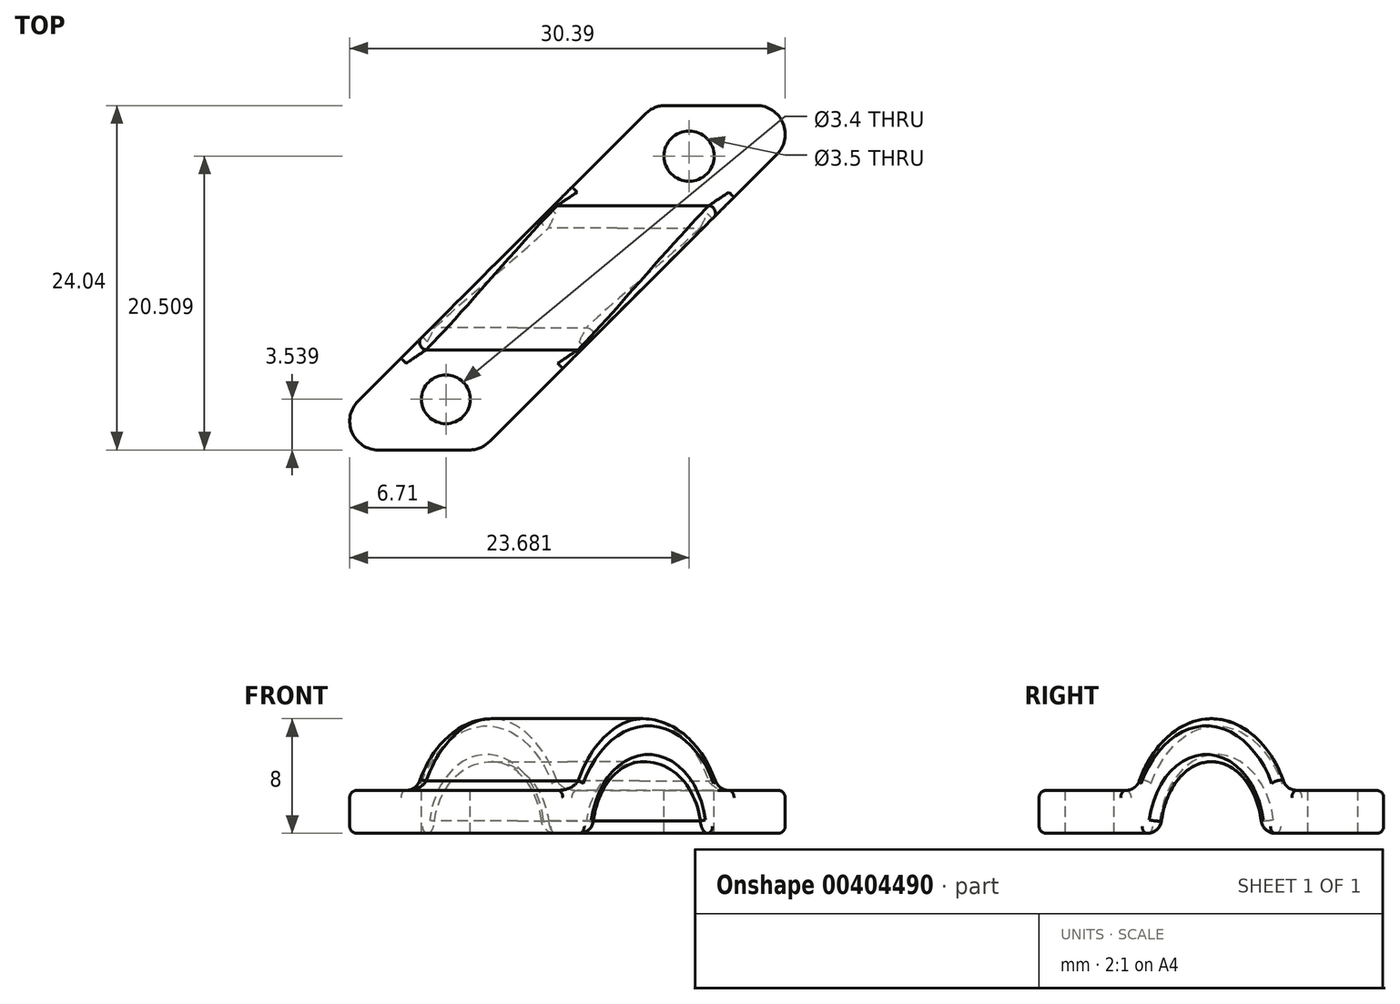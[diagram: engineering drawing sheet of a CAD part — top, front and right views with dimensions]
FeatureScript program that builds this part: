
annotation { "Feature Type Name" : "Feature", "Feature Type Description" : "" }
export const myFeature = defineFeature(function(context is Context, id is Id, definition is map)
    precondition{}
    {
        {
            var Q0;
            Q0=qCreatedBy(makeId("Top.planeOp"),FACE);
            var sketch = newSketch(context, id + "F0", { "sketchPlane" : qUnion([Q0])});
            skLineSegment(sketch, "E0", {"start": v(0, -18.35) * mm, "end": v(0, 0) * mm, "construction": true});
            skLineSegment(sketch, "E1", {"start": v(0, 0) * mm, "end": v(0, 0) * mm});
            skLineSegment(sketch, "E2", {"start": v(0, 0) * mm, "end": v(30, 30) * mm, "construction": true});
            skCircle(sketch, "E3", {"center": v(15, 8.92) * mm, "radius": 1.7 * mm});
            skPoint(sketch, "E3.centerSnap0", {"position": v(15, 15) * mm});
            skCircle(sketch, "E4", {"center": v(31.97, 25.89) * mm, "radius": 1.75 * mm});
            skLineSegment(sketch, "E5", {"start": v(6.42, 0.34) * mm, "end": v(37.39, 31.3) * mm, "construction": true});
            skLineSegment(sketch, "E6", {"start": v(21, 8.92) * mm, "end": v(15, 8.92) * mm});
            skLineSegment(sketch, "E7", {"start": v(15, 8.92) * mm, "end": v(9, 8.92) * mm});
            skSolve(sketch);
        }
        {
            var Q0;
            Q0=sQuery(id+"F0.wireOp",EDGE,"E5");
            var Q1;
            Q1=qCreatedBy(makeId("Top.planeOp"),FACE);
            cPlane(context, id + "F1", {"entities" : qUnion([Q0, Q1]), "cplaneType" : CPlaneType.LINE_ANGLE, "offset" : 25 * mm, "angle" : 90 * degree, "width" : 150 * mm, "height" : 150 * mm});
        }
        {
            var Q0;
            Q0=qCreatedBy(id+"F1.planeOp",FACE);
            var sketch = newSketch(context, id + "F2", { "sketchPlane" : qUnion([Q0])});
            skPoint(sketch, "E8.0", {"position": v(-16.91, 0) * mm});
            skPoint(sketch, "E9.0", {"position": v(-40.91, 0) * mm});
            skLineSegment(sketch, "E10", {"start": v(-40.91, 0) * mm, "end": v(-40.91, 4.4) * mm, "construction": true});
            skLineSegment(sketch, "E11", {"start": v(-16.91, 0) * mm, "end": v(-16.91, 4.43) * mm, "construction": true});
            skLineSegment(sketch, "E12.bottom", {"start": v(-11.91, 3) * mm, "end": v(-21.5, 3) * mm});
            skLineSegment(sketch, "E12.top", {"start": v(-11.91, 0) * mm, "end": v(-23.91, 0) * mm});
            skLineSegment(sketch, "E12.left", {"start": v(-11.91, 3) * mm, "end": v(-11.91, 0) * mm});
            skLineSegment(sketch, "E12.right", {"start": v(-45.91, 3) * mm, "end": v(-45.91, 0) * mm});
            skArc(sketch, "E13", {"start": v(-23.91, 0) * mm, "mid": v(-28.91, 5) * mm, "end": v(-33.91, 0) * mm});
            skArc(sketch, "E14", {"start": v(-21.5, 3) * mm, "mid": v(-28.91, 8) * mm, "end": v(-36.33, 3) * mm});
            skLineSegment(sketch, "E15.trimOffspring", {"start": v(-33.91, 0) * mm, "end": v(-45.91, 0) * mm});
            skLineSegment(sketch, "E16.trimOffspring", {"start": v(-36.33, 3) * mm, "end": v(-45.91, 3) * mm});
            skSolve(sketch);
        }
        {
            var Q0;
            Q0 = qSketchRegion(id + "F2", true);
            var Q1;
            Q1=sQuery(id+"F0.wireOp",EDGE,"E6");
            sweep(context, id + "F3", {"profiles" : qUnion([Q0]), "path" : qUnion([Q1])});
        }
        {
            var Q0;
            Q0 = qSketchRegion(id + "F2", true);
            var Q1;
            Q1=sQuery(id+"F0.wireOp",EDGE,"E7");
            sweep(context, id + "F4", {"operationType" : NewBodyOperationType.ADD, "profiles" : qUnion([Q0]), "path" : qUnion([Q1])});
        }
        {
            var Q0;
            {var subQ0=sQuery(id+"F2.wireOp",EDGE,"E12.bottom");Q0=makeQuery(id+"F4.boolean.opBoolean","MERGE",FACE,{"derivedFrom":[makeQuery(id+"F3.opSweep","SWEPT_FACE",FACE,{"disambiguationData":[OSD([sQuery(id+"F0.wireOp",EDGE,"E6"),subQ0])]}),makeQuery(id+"F4.opSweep","SWEPT_FACE",FACE,{"disambiguationData":[OSD([sQuery(id+"F0.wireOp",EDGE,"E7"),subQ0])]})]});}
            var sketch = newSketch(context, id + "F5", { "sketchPlane" : qUnion([Q0])});
            skCircle(sketch, "E17.0", {"center": v(15, 8.92) * mm, "radius": 1.7 * mm});
            skCircle(sketch, "E18.0", {"center": v(31.97, 25.89) * mm, "radius": 1.75 * mm});
            skSolve(sketch);
        }
        {
            var Q0;
            Q0=makeQuery(id+"F5.imprint","IMPRINT",FACE,{"disambiguationData":[TD([[makeQuery(id+"F5.imprint","IMPRINT",EDGE,{"derivedFrom":sQuery(id+"F5.wireOp",EDGE,"E17.0")}),1.0]])]});
            var Q1;
            Q1=makeQuery(id+"F5.imprint","IMPRINT",FACE,{"disambiguationData":[TD([[makeQuery(id+"F5.imprint","IMPRINT",EDGE,{"derivedFrom":sQuery(id+"F5.wireOp",EDGE,"E18.0")}),1.0]])]});
            extrude(context, id + "F6", {"entities" : qUnion([Q0, Q1]), "operationType" : NewBodyOperationType.REMOVE, "oppositeDirection" : true, "depth" : 25 * mm});
        }
        {
            var Q0;
            Q0=makeQuery(id+"F3.opSweep","SWEPT_EDGE",EDGE,{"disambiguationData":[OSD([sQuery(id+"F0.wireOp",EDGE,"E6"),sQuery(id+"F2.wireOp",EDGE,"E13"),sQuery(id+"F2.wireOp",EDGE,"E15.trimOffspring")])]});
            var Q1;
            Q1=makeQuery(id+"F3.opSweep","SWEPT_EDGE",EDGE,{"disambiguationData":[OSD([sQuery(id+"F0.wireOp",EDGE,"E6"),sQuery(id+"F2.wireOp",EDGE,"E12.top"),sQuery(id+"F2.wireOp",EDGE,"E13")])]});
            var Q2;
            Q2=makeQuery(id+"F3.opSweep","SWEPT_EDGE",EDGE,{"disambiguationData":[OSD([sQuery(id+"F0.wireOp",EDGE,"E6"),sQuery(id+"F2.wireOp",EDGE,"E14"),sQuery(id+"F2.wireOp",EDGE,"E16.trimOffspring")])]});
            var Q3;
            Q3=makeQuery(id+"F4.opSweep","SWEPT_EDGE",EDGE,{"disambiguationData":[OSD([sQuery(id+"F0.wireOp",EDGE,"E7"),sQuery(id+"F2.wireOp",EDGE,"E12.bottom"),sQuery(id+"F2.wireOp",EDGE,"E14")])]});
            fillet(context, id + "F7", {"entities" : qUnion([Q0, Q1, Q2, Q3]), "radius" : 1 * mm, "tangentPropagation" : true, "allowEdgeOverflow" : false});
        }
        {
            var Q0;
            Q0=makeQuery(id+"F3.opSweep","CAP_EDGE",EDGE,{"disambiguationData":[OSD([sQuery(id+"F0.wireOp",VERTEX,"E6.start"),sQuery(id+"F2.wireOp",EDGE,"E12.right")])],"isStart":false});
            var Q1;
            Q1=makeQuery(id+"F4.opSweep","CAP_EDGE",EDGE,{"disambiguationData":[OSD([sQuery(id+"F0.wireOp",VERTEX,"E7.end"),sQuery(id+"F2.wireOp",EDGE,"E12.left")])],"isStart":false});
            var Q2;
            Q2=makeQuery(id+"F3.opSweep","CAP_EDGE",EDGE,{"disambiguationData":[OSD([sQuery(id+"F0.wireOp",VERTEX,"E6.start"),sQuery(id+"F2.wireOp",EDGE,"E12.left")])],"isStart":false});
            var Q3;
            Q3=makeQuery(id+"F4.opSweep","CAP_EDGE",EDGE,{"disambiguationData":[OSD([sQuery(id+"F0.wireOp",VERTEX,"E7.end"),sQuery(id+"F2.wireOp",EDGE,"E12.right")])],"isStart":false});
            fillet(context, id + "F8", {"entities" : qUnion([Q0, Q1, Q2, Q3]), "radius" : 2 * mm, "tangentPropagation" : true, "allowEdgeOverflow" : false});
        }
        {
            var Q0;
            Q0=makeQuery(id+"F3.opSweep","CAP_EDGE",EDGE,{"disambiguationData":[OSD([sQuery(id+"F0.wireOp",VERTEX,"E6.start"),sQuery(id+"F2.wireOp",EDGE,"E12.top")])],"isStart":false});
            var Q1;
            Q1=makeQuery(id+"F3.opSweep","CAP_EDGE",EDGE,{"disambiguationData":[OSD([sQuery(id+"F0.wireOp",VERTEX,"E6.start"),sQuery(id+"F2.wireOp",EDGE,"E14")])],"isStart":false});
            var Q2;
            Q2=makeQuery(id+"F4.opSweep","CAP_EDGE",EDGE,{"disambiguationData":[OSD([sQuery(id+"F0.wireOp",VERTEX,"E7.end"),sQuery(id+"F2.wireOp",EDGE,"E12.bottom")])],"isStart":false});
            fillet(context, id + "F9", {"entities" : qUnion([Q0, Q1, Q2]), "radius" : 0.5 * mm, "tangentPropagation" : true, "allowEdgeOverflow" : false});
        }
    });
